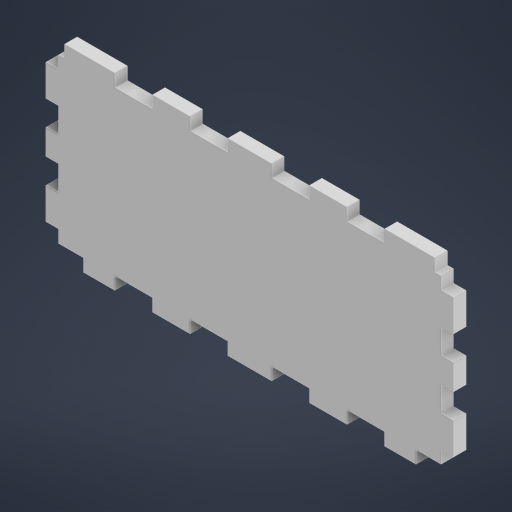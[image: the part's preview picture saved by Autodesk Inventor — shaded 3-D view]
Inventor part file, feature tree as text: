
AUTODESK INVENTOR PART (.ipt)
format: ipt  version: 2023.2 (Build 272271000, 271)  size: 349,184 bytes
history: native  units: mm
features: sketch x2
ambient origin geometry x8: Origin, YZ Plane, XZ Plane, XY Plane, X Axis, Y Axis, Z Axis, Center Point
bodies: Body1 (feature_tree)
feature tree (2):
  sketch  "Sketch1"  dims[d228=130.0mm]
  sketch  "Sketch2"  dims[d229=60.0mm d230=4.0mm d231=0.0mm d234=10.0mm d235=12.0mm d236=12.0mm d237=12.0mm d238=14.0mm d240=12.0mm d242=12.0mm d243=10.0mm d244=12.0mm d245=12.0mm d246=12.0mm d249=8.0mm d251=8.0mm d255=8.0mm d259=4.0mm d260=0.0mm d262=4.0mm d267=8.0mm d268=10.0mm d271=10.0mm d272=8.0mm d273=6.0mm d9=0.5mm d10=0.872665mm d11=0.5mm d12=0.872665mm d13=0.5mm d14=0.872665mm d27=0.5mm d28=0.872665mm d29=0.5mm d30=0.872665mm d88=0.5mm d89=0.872665mm d90=0.5mm d91=0.872665mm d116=0.5mm d117=0.872665mm d118=0.5mm d119=0.872665mm d154=0.5mm d155=0.872665mm d156=0.5mm d157=0.872665mm d181=0.5mm d182=0.872665mm d183=0.5mm d184=0.872665mm d221=0.5mm d222=0.872665mm d223=0.5mm d224=0.872665mm]
